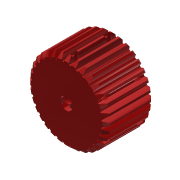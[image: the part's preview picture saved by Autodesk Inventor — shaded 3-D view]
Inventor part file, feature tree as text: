
AUTODESK INVENTOR PART (.ipt)
format: ipt  version: 2019.4 (Build 234330000, 330)  size: 671,232 bytes
history: native  units: mm (DEFAULTED — no unit token found)
features: other x5, sketch x5, extrude x3, plane x3, revolve x1, pattern_circular x1, pattern_linear x1, reference x1, projected_geometry x1
ambient origin geometry x8: Origin, YZ Plane, XZ Plane, XY Plane, X Axis, Y Axis, Z Axis, Center Point
bodies: Solid1 (feature_tree)
feature tree (21):
  extrude  "Extrusion1"  Depth=20.0mm TaperAngle=0.0deg
  plane  "Work Plane2"
  plane  "Work Plane8"
  plane  "Work Plane9"
  other  "Spur Gear"
  extrude  "Extrusion2"  Depth=10.0mm TaperAngle=0.0deg
  revolve  "Revolution1"  [1 undecoded]
  extrude  "Extrusion3"  TaperAngle=0.0deg  [1 undecoded]
  pattern_circular  "Circular Pattern1"  [2 undecoded]
  pattern_linear  "Rectangular Pattern1"  Spacing1=0.0mm  [1 undecoded]
  sketch  "Sketch1"  dims[d0=34.0mm d1=20.0mm d2=0.0mm]
  sketch  "Sketch2"  dims[d3=32.0mm d4=10.0mm d5=0.0mm]
  other  "Srf1"
  sketch  "Sketch3"  dims[d16=29.5mm d17=0.0mm d34=0.981748mm]
  reference  "Reference1"
  sketch  "Sketch4"  dims[d39=0.0mm d41=0.0mm]
  sketch  "Sketch5"  dims[d43=29.5mm d46=29.5mm d47=0.0mm d48=0.0mm d49=0.1mm d50=10.0mm d51=0.0mm d52=45.0deg d53=90.0deg d54=2.8mm d55=10.0mm d56=0.0mm d57=60.0mm d58=360.0deg d60=20.0mm d62=14.0mm]
  projected_geometry  "Projected Loop1"
  other  "Pitch Diameter"
  other  "Assembly_Cube_Z_stage_sample_outercube_NEMA_motorized.iam"
  other  "00_NEMA11:1"
note: 5 required parameter values undecoded (feature->parameter linkage not recoverable at this tier; creation-order binding heuristic only, values carry confidence <= 0.55)